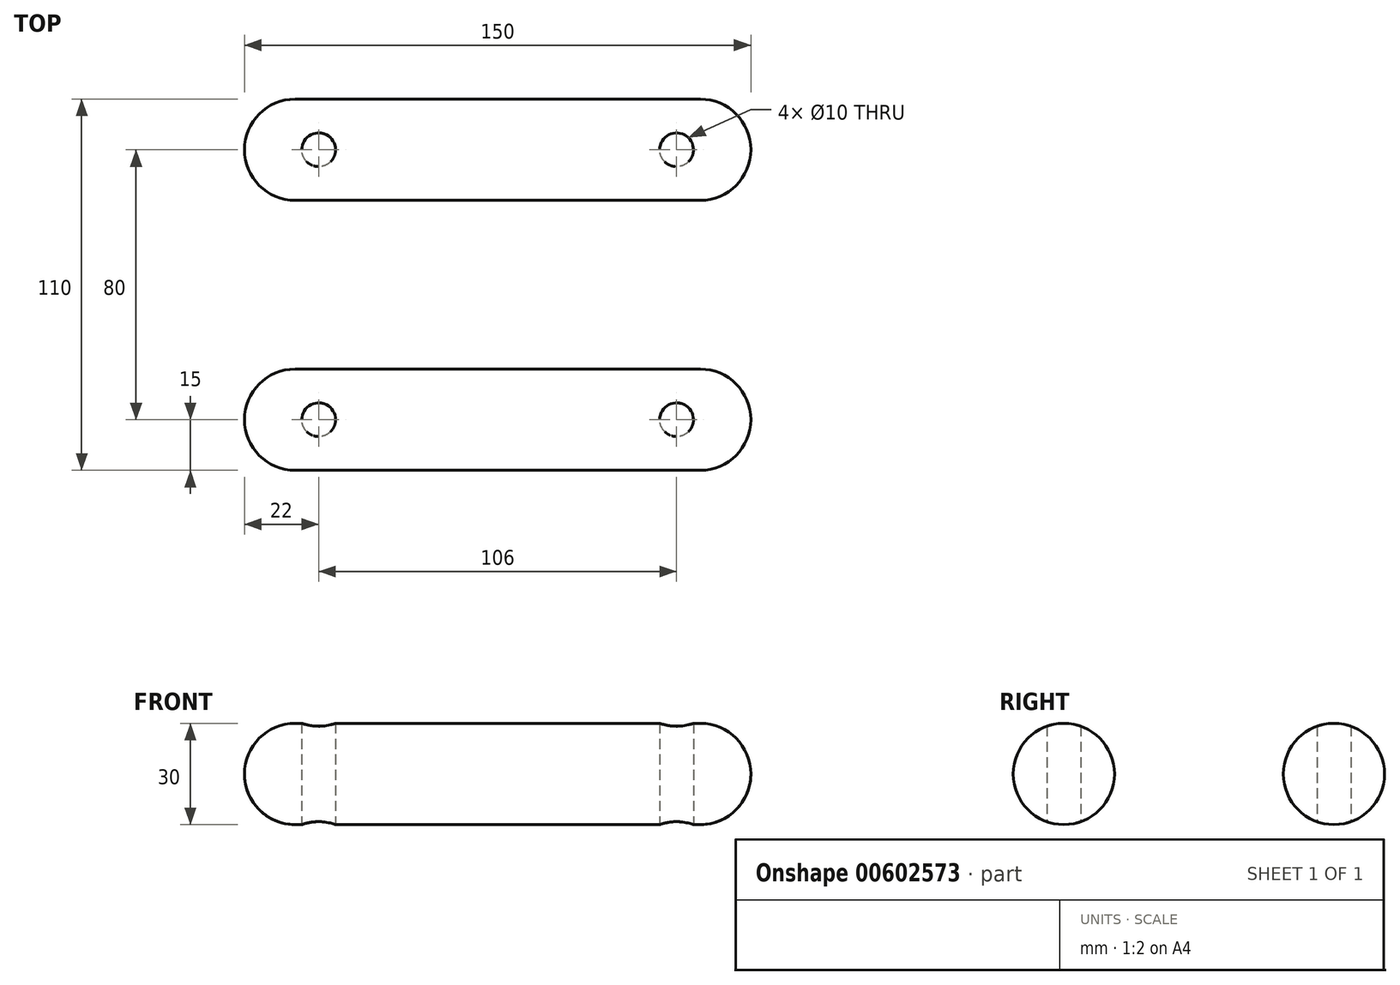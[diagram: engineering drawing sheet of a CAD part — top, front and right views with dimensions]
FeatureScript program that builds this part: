
annotation { "Feature Type Name" : "Feature", "Feature Type Description" : "" }
export const myFeature = defineFeature(function(context is Context, id is Id, definition is map)
    precondition{}
    {
        {
            var Q0;
            Q0=qCreatedBy(makeId("Right.planeOp"),FACE);
            var sketch = newSketch(context, id + "F0", { "sketchPlane" : qUnion([Q0])});
            skCircle(sketch, "E0", {"center": v(-40, 0) * mm, "radius": 15 * mm});
            skCircle(sketch, "E1", {"center": v(40, 0) * mm, "radius": 15 * mm});
            skSolve(sketch);
        }
        {
            var Q0;
            Q0=makeQuery(id+"F0.imprint","IMPRINT",FACE,{"disambiguationData":[TD([[makeQuery(id+"F0.imprint","IMPRINT",EDGE,{"derivedFrom":sQuery(id+"F0.wireOp",EDGE,"E0")}),1.0]])]});
            var Q1;
            Q1=makeQuery(id+"F0.imprint","IMPRINT",FACE,{"disambiguationData":[TD([[makeQuery(id+"F0.imprint","IMPRINT",EDGE,{"derivedFrom":sQuery(id+"F0.wireOp",EDGE,"E1")}),1.0]])]});
            extrude(context, id + "F1", {"entities" : qUnion([Q0, Q1]), "endBound" : BoundingType.SYMMETRIC, "depth" : 150 * mm, "offsetDistance" : 25 * mm});
        }
        {
            var Q0;
            Q0=makeQuery(id+"F1.opExtrude","CAP_FACE",FACE,{"disambiguationData":[OSD([sQuery(id+"F0.wireOp",EDGE,"E0")])],"isStart":false});
            var Q1;
            Q1=makeQuery(id+"F1.opExtrude","CAP_FACE",FACE,{"disambiguationData":[OSD([sQuery(id+"F0.wireOp",EDGE,"E1")])],"isStart":false});
            var Q2;
            Q2=makeQuery(id+"F1.opExtrude","CAP_FACE",FACE,{"disambiguationData":[OSD([sQuery(id+"F0.wireOp",EDGE,"E0")])],"isStart":true});
            var Q3;
            Q3=makeQuery(id+"F1.opExtrude","CAP_FACE",FACE,{"disambiguationData":[OSD([sQuery(id+"F0.wireOp",EDGE,"E1")])],"isStart":true});
            fillet(context, id + "F2", {"entities" : qUnion([Q0, Q1, Q2, Q3]), "radius" : 15 * mm, "tangentPropagation" : true, "allowEdgeOverflow" : false});
        }
        {
            var Q0;
            Q0=qCreatedBy(makeId("Top.planeOp"),FACE);
            var sketch = newSketch(context, id + "F3", { "sketchPlane" : qUnion([Q0])});
            skCircle(sketch, "E2", {"center": v(-53, 40) * mm, "radius": 5 * mm});
            skCircle(sketch, "E3", {"center": v(53, 40) * mm, "radius": 5 * mm});
            skCircle(sketch, "E4", {"center": v(53, -40) * mm, "radius": 5 * mm});
            skCircle(sketch, "E5", {"center": v(-53, -40) * mm, "radius": 5 * mm});
            skSolve(sketch);
        }
        {
            var Q0;
            Q0=makeQuery(id+"F3.imprint","IMPRINT",FACE,{"disambiguationData":[TD([[makeQuery(id+"F3.imprint","IMPRINT",EDGE,{"derivedFrom":sQuery(id+"F3.wireOp",EDGE,"E2")}),1.0]])]});
            var Q1;
            Q1=makeQuery(id+"F3.imprint","IMPRINT",FACE,{"disambiguationData":[TD([[makeQuery(id+"F3.imprint","IMPRINT",EDGE,{"derivedFrom":sQuery(id+"F3.wireOp",EDGE,"E5")}),1.0]])]});
            var Q2;
            Q2=makeQuery(id+"F3.imprint","IMPRINT",FACE,{"disambiguationData":[TD([[makeQuery(id+"F3.imprint","IMPRINT",EDGE,{"derivedFrom":sQuery(id+"F3.wireOp",EDGE,"E4")}),1.0]])]});
            var Q3;
            Q3=makeQuery(id+"F3.imprint","IMPRINT",FACE,{"disambiguationData":[TD([[makeQuery(id+"F3.imprint","IMPRINT",EDGE,{"derivedFrom":sQuery(id+"F3.wireOp",EDGE,"E3")}),1.0]])]});
            extrude(context, id + "F4", {"entities" : qUnion([Q0, Q1, Q2, Q3]), "operationType" : NewBodyOperationType.REMOVE, "endBound" : BoundingType.SYMMETRIC, "depth" : 30 * mm, "offsetDistance" : 25 * mm});
        }
    });
